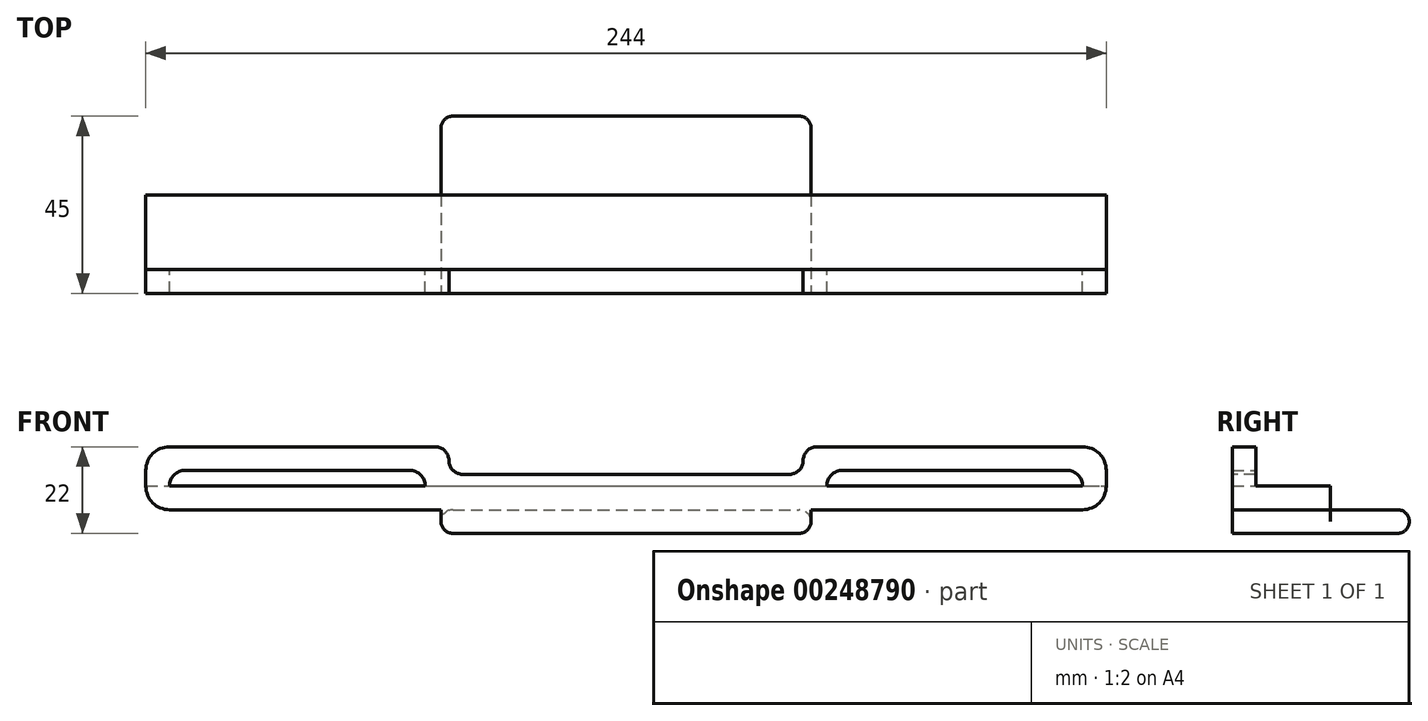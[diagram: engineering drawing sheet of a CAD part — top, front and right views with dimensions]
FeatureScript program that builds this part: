
annotation { "Feature Type Name" : "Feature", "Feature Type Description" : "" }
export const myFeature = defineFeature(function(context is Context, id is Id, definition is map)
    precondition{}
    {
        {
            var Q0;
            Q0=qCreatedBy(makeId("Front.planeOp"),FACE);
            var sketch = newSketch(context, id + "F0", { "sketchPlane" : qUnion([Q0])});
            skLineSegment(sketch, "E0", {"start": v(-122, 0) * mm, "end": v(-122, 22) * mm});
            skLineSegment(sketch, "E1.MirrorCS", {"start": v(122, 0) * mm, "end": v(122, 22) * mm});
            skLineSegment(sketch, "E2", {"start": v(-122, 0) * mm, "end": v(122, 0) * mm});
            skLineSegment(sketch, "E3", {"start": v(-122, 22) * mm, "end": v(122, 22) * mm});
            skLineSegment(sketch, "E4", {"start": v(-122, 6) * mm, "end": v(122, 6) * mm});
            skLineSegment(sketch, "E5", {"start": v(-47, 6) * mm, "end": v(-47, 0) * mm});
            skLineSegment(sketch, "E6.MirrorCS", {"start": v(47, 6) * mm, "end": v(47, 0) * mm});
            skLineSegment(sketch, "E7", {"start": v(-122, 12) * mm, "end": v(122, 12) * mm});
            skLineSegment(sketch, "E8", {"start": v(-45, 22) * mm, "end": v(-45, 15) * mm});
            skLineSegment(sketch, "E9.MirrorCS", {"start": v(45, 22) * mm, "end": v(45, 15) * mm});
            skLineSegment(sketch, "E10", {"start": v(-45, 15) * mm, "end": v(45, 15) * mm});
            skSolve(sketch);
        }
        {
            var Q0;
            {var subQ7=sQuery(id+"F0.wireOp",EDGE,"E7");Q0=makeQuery(id+"F0.imprint","IMPRINT",FACE,{"disambiguationData":[TD([[makeQuery(id+"F0.imprint","IMPRINT",EDGE,{"derivedFrom":subQ7}),1.0]])]});}
            extrude(context, id + "F1", {"entities" : qUnion([Q0]), "oppositeDirection" : true, "depth" : 6 * mm, "offsetDistance" : 25 * mm});
        }
        {
            var Q0;
            {var subQ5=sQuery(id+"F0.wireOp",EDGE,"E7");Q0=makeQuery(id+"F0.imprint","IMPRINT",FACE,{"disambiguationData":[TD([[makeQuery(id+"F0.imprint","IMPRINT",EDGE,{"derivedFrom":subQ5}),-1.0]])]});}
            extrude(context, id + "F2", {"entities" : qUnion([Q0]), "operationType" : NewBodyOperationType.ADD, "oppositeDirection" : true, "depth" : 25 * mm, "offsetDistance" : 25 * mm});
        }
        {
            var Q0;
            {var subQ0=sQuery(id+"F0.wireOp",EDGE,"E5");Q0=makeQuery(id+"F0.imprint","IMPRINT",FACE,{"disambiguationData":[TD([[makeQuery(id+"F0.imprint","IMPRINT",EDGE,{"derivedFrom":subQ0}),1.0]])]});}
            var Q1;
            Q1=makeQuery(id+"F2.opExtrude","CAP_FACE",FACE,{"disambiguationData":[OSD([sQuery(id+"F0.wireOp",EDGE,"E0"),sQuery(id+"F0.wireOp",EDGE,"E1.MirrorCS"),sQuery(id+"F0.wireOp",EDGE,"E4"),sQuery(id+"F0.wireOp",EDGE,"E7")])],"isStart":false});
            extrude(context, id + "F3", {"entities" : qUnion([Q0]), "operationType" : NewBodyOperationType.ADD, "endBound" : BoundingType.UP_TO_SURFACE, "oppositeDirection" : true, "depth" : 25 * mm, "endBoundEntityFace" : qUnion([Q1]), "hasOffset" : true, "offsetDistance" : 20 * mm, "offsetOppositeDirection" : true});
        }
        {
            var Q0;
            Q0=makeQuery(id+"F1.opExtrude","CAP_FACE",FACE,{"disambiguationData":[OSD([sQuery(id+"F0.wireOp",EDGE,"E0"),sQuery(id+"F0.wireOp",EDGE,"E1.MirrorCS"),sQuery(id+"F0.wireOp",EDGE,"E3"),sQuery(id+"F0.wireOp",EDGE,"E7"),sQuery(id+"F0.wireOp",EDGE,"E8"),sQuery(id+"F0.wireOp",EDGE,"E9.MirrorCS"),sQuery(id+"F0.wireOp",EDGE,"E10")])],"isStart":false});
            var sketch = newSketch(context, id + "F4", { "sketchPlane" : qUnion([Q0])});
            skLineSegment(sketch, "E11", {"start": v(51, 12) * mm, "end": v(51, 16) * mm});
            skLineSegment(sketch, "E12", {"start": v(51, 16) * mm, "end": v(116, 16) * mm});
            skLineSegment(sketch, "E13", {"start": v(116, 16) * mm, "end": v(116, 12) * mm});
            skLineSegment(sketch, "E14.MirrorCS", {"start": v(-51, 12) * mm, "end": v(-51, 16) * mm});
            skLineSegment(sketch, "E15.MirrorCS", {"start": v(-51, 16) * mm, "end": v(-116, 16) * mm});
            skLineSegment(sketch, "E16.MirrorCS", {"start": v(-116, 16) * mm, "end": v(-116, 12) * mm});
            skSolve(sketch);
        }
        {
            var Q0;
            {var subQ0=sQuery(id+"F4.wireOp",EDGE,"E11");Q0=makeQuery(id+"F4.imprint","IMPRINT",FACE,{"disambiguationData":[TD([[makeQuery(id+"F4.imprint","IMPRINT",EDGE,{"derivedFrom":subQ0}),-1.0]])]});}
            var Q1;
            {var subQ0=sQuery(id+"F4.wireOp",EDGE,"E14.MirrorCS");Q1=makeQuery(id+"F4.imprint","IMPRINT",FACE,{"disambiguationData":[TD([[makeQuery(id+"F4.imprint","IMPRINT",EDGE,{"derivedFrom":subQ0}),1.0]])]});}
            extrude(context, id + "F5", {"entities" : qUnion([Q0, Q1]), "operationType" : NewBodyOperationType.REMOVE, "oppositeDirection" : true, "depth" : 25 * mm, "offsetDistance" : 25 * mm});
        }
        {
            var Q0;
            Q0=makeQuery(id+"F5.boolean.opBoolean","COPY",EDGE,{"derivedFrom":makeQuery(id+"F5.opExtrude","SWEPT_EDGE",EDGE,{"disambiguationData":[OSD([sQuery(id+"F4.wireOp",EDGE,"E11"),sQuery(id+"F4.wireOp",EDGE,"E12")])]})});
            var Q1;
            Q1=makeQuery(id+"F5.boolean.opBoolean","COPY",EDGE,{"derivedFrom":makeQuery(id+"F5.opExtrude","SWEPT_EDGE",EDGE,{"disambiguationData":[OSD([sQuery(id+"F4.wireOp",EDGE,"E12"),sQuery(id+"F4.wireOp",EDGE,"E13")])]})});
            var Q2;
            Q2=makeQuery(id+"F5.boolean.opBoolean","COPY",EDGE,{"derivedFrom":makeQuery(id+"F5.opExtrude","SWEPT_EDGE",EDGE,{"disambiguationData":[OSD([sQuery(id+"F4.wireOp",EDGE,"E14.MirrorCS"),sQuery(id+"F4.wireOp",EDGE,"E15.MirrorCS")])]})});
            var Q3;
            Q3=makeQuery(id+"F5.boolean.opBoolean","COPY",EDGE,{"derivedFrom":makeQuery(id+"F5.opExtrude","SWEPT_EDGE",EDGE,{"disambiguationData":[OSD([sQuery(id+"F4.wireOp",EDGE,"E15.MirrorCS"),sQuery(id+"F4.wireOp",EDGE,"E16.MirrorCS")])]})});
            fillet(context, id + "F6", {"entities" : qUnion([Q0, Q1, Q2, Q3]), "tangentPropagation" : true, "radius" : 4 * mm, "defaultsChanged" : false, "vertexSettings" : [], "allowEdgeOverflow" : false});
        }
        {
            var Q0;
            Q0=makeQuery(id+"F1.opExtrude","SWEPT_EDGE",EDGE,{"disambiguationData":[OSD([sQuery(id+"F0.wireOp",EDGE,"E8"),sQuery(id+"F0.wireOp",EDGE,"E10")])]});
            var Q1;
            Q1=makeQuery(id+"F1.opExtrude","SWEPT_EDGE",EDGE,{"disambiguationData":[OSD([sQuery(id+"F0.wireOp",EDGE,"E3"),sQuery(id+"F0.wireOp",EDGE,"E8")])]});
            var Q2;
            Q2=makeQuery(id+"F1.opExtrude","SWEPT_EDGE",EDGE,{"disambiguationData":[OSD([sQuery(id+"F0.wireOp",EDGE,"E9.MirrorCS"),sQuery(id+"F0.wireOp",EDGE,"E10")])]});
            var Q3;
            Q3=makeQuery(id+"F1.opExtrude","SWEPT_EDGE",EDGE,{"disambiguationData":[OSD([sQuery(id+"F0.wireOp",EDGE,"E3"),sQuery(id+"F0.wireOp",EDGE,"E9.MirrorCS")])]});
            fillet(context, id + "F7", {"entities" : qUnion([Q0, Q1, Q2, Q3]), "tangentPropagation" : true, "radius" : 3.5 * mm, "defaultsChanged" : true, "vertexSettings" : [], "allowEdgeOverflow" : false});
        }
        {
            var Q0;
            Q0=makeQuery(id+"F1.opExtrude","SWEPT_EDGE",EDGE,{"disambiguationData":[OSD([sQuery(id+"F0.wireOp",EDGE,"E0"),sQuery(id+"F0.wireOp",EDGE,"E3")])]});
            var Q1;
            Q1=makeQuery(id+"F1.opExtrude","SWEPT_EDGE",EDGE,{"disambiguationData":[OSD([sQuery(id+"F0.wireOp",EDGE,"E1.MirrorCS"),sQuery(id+"F0.wireOp",EDGE,"E3")])]});
            var Q2;
            Q2=makeQuery(id+"F2.opExtrude","SWEPT_EDGE",EDGE,{"disambiguationData":[OSD([sQuery(id+"F0.wireOp",EDGE,"E0"),sQuery(id+"F0.wireOp",EDGE,"E4")])]});
            var Q3;
            Q3=makeQuery(id+"F2.opExtrude","SWEPT_EDGE",EDGE,{"disambiguationData":[OSD([sQuery(id+"F0.wireOp",EDGE,"E1.MirrorCS"),sQuery(id+"F0.wireOp",EDGE,"E4")])]});
            fillet(context, id + "F8", {"entities" : qUnion([Q0, Q1, Q2, Q3]), "tangentPropagation" : true, "radius" : 6 * mm, "defaultsChanged" : false, "vertexSettings" : [], "allowEdgeOverflow" : false});
        }
        {
            var Q0;
            {var subQ0=sQuery(id+"F0.wireOp",EDGE,"E4");var subQ1=sQuery(id+"F0.wireOp",EDGE,"E6.MirrorCS");Q0=makeQuery(id+"F3.boolean.opBoolean","SPLIT",EDGE,{"disambiguationData":[topologyDisambiguationEdgeConnected([makeQuery(id+"F2.opExtrude","SWEPT_FACE",FACE,{"disambiguationData":[OSD([subQ0])]})])],"derivedFrom":makeQuery(id+"F3.opExtrude","SWEPT_EDGE",EDGE,{"disambiguationData":[OSD([subQ0,subQ1])]})});}
            var Q1;
            Q1=makeQuery(id+"F3.opExtrude","SWEPT_EDGE",EDGE,{"disambiguationData":[OSD([sQuery(id+"F0.wireOp",EDGE,"E2"),sQuery(id+"F0.wireOp",EDGE,"E6.MirrorCS")])]});
            var Q2;
            Q2=makeQuery(id+"F3.opExtrude","SWEPT_EDGE",EDGE,{"disambiguationData":[OSD([sQuery(id+"F0.wireOp",EDGE,"E2"),sQuery(id+"F0.wireOp",EDGE,"E5")])]});
            var Q3;
            {var subQ0=sQuery(id+"F0.wireOp",EDGE,"E4");var subQ1=sQuery(id+"F0.wireOp",EDGE,"E5");Q3=makeQuery(id+"F3.boolean.opBoolean","SPLIT",EDGE,{"disambiguationData":[topologyDisambiguationEdgeConnected([makeQuery(id+"F2.opExtrude","SWEPT_FACE",FACE,{"disambiguationData":[OSD([subQ0])]})])],"derivedFrom":makeQuery(id+"F3.opExtrude","SWEPT_EDGE",EDGE,{"disambiguationData":[OSD([subQ0,subQ1])]})});}
            fillet(context, id + "F9", {"entities" : qUnion([Q0, Q1, Q2, Q3]), "tangentPropagation" : true, "radius" : 3 * mm, "defaultsChanged" : false, "vertexSettings" : [], "allowEdgeOverflow" : false});
        }
        {
            var Q0;
            Q0=makeQuery(id+"F3.opExtrude","CAP_EDGE",EDGE,{"disambiguationData":[OSD([sQuery(id+"F0.wireOp",EDGE,"E2")])],"isStart":false});
            var Q1;
            Q1=makeQuery(id+"F3.opExtrude","CAP_EDGE",EDGE,{"disambiguationData":[OSD([sQuery(id+"F0.wireOp",EDGE,"E4")])],"isStart":false});
            fillet(context, id + "F10", {"entities" : qUnion([Q0, Q1]), "tangentPropagation" : true, "radius" : 3 * mm, "defaultsChanged" : true, "vertexSettings" : [], "allowEdgeOverflow" : false});
        }
    });
